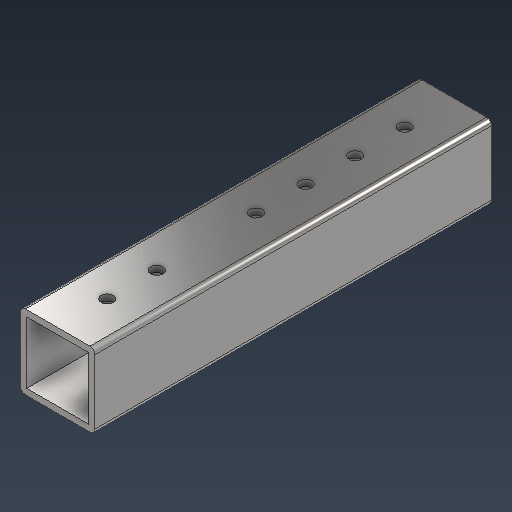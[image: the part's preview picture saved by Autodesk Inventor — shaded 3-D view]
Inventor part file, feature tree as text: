
AUTODESK INVENTOR PART (.ipt)
format: ipt  version: 2021 (Build 250183000, 183)  size: 237,056 bytes
history: native  units: mm
features: sketch x3, hole x2, extrude x1, fillet x1, plane x1, split x1, pattern_linear x1
ambient origin geometry x8: Origin, YZ Plane, XZ Plane, XY Plane, X Axis, Y Axis, Z Axis, Center Point
bodies: Solid1 (feature_tree)
feature tree (10):
  extrude  "Extrusion1"  Depth=30.0mm
  fillet  "Fillet1"  Radius=15.0mm
  plane  "Work Plane1"
  split  "Split1"
  hole  "Hole1"  [1 undecoded]
  pattern_linear  "Rectangular Pattern1"  Count1=100 Spacing1=0.0mm
  hole  "Hole2"  [1 undecoded]
  sketch  "Sketch1"  dims[d0=30.0mm d1=30.0mm d2=15.0mm]
  sketch  "Sketch2"  dims[d3=15.0mm d4=2.5mm d5=1000.0mm d6=0.0mm]
  sketch  "Sketch3"  dims[d7=2.0mm d8=-160.0mm d9=0.0mm d10=20.0mm d11=5.0mm d12=6.0mm d13=4.0mm d14=2.0mm d15=90.0deg d16=8.0mm d17=20.594885mm d18=40.0mm d20=20.0mm d21=20.0mm d22=0.0mm d23=5.0mm d24=6.0mm d25=4.0mm d26=2.0mm d27=90.0deg d28=8.0mm d29=20.594885mm d30=0.0mm d31=20.0mm]
note: 2 required parameter values undecoded (feature->parameter linkage not recoverable at this tier; creation-order binding heuristic only, values carry confidence <= 0.55)
